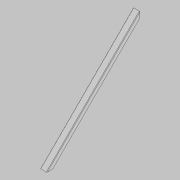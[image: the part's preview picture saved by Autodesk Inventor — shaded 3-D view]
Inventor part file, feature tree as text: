
AUTODESK INVENTOR PART (.ipt)
format: ipt  version: 2021 (Build 250183000, 183)  size: 105,472 bytes
history: native  units: mm
features: sweep x1, fillet x1, mirror x1, split x1, other x1, sketch x1
ambient origin geometry x8: Origin, YZ Plane, XZ Plane, XY Plane, X Axis, Y Axis, Z Axis, Center Point
bodies: Solid1 (feature_tree)
feature tree (6):
  sweep  "Sweep1"
  fillet  "Fillet1"  Radius=25.0mm
  mirror  "mirrored45"
  split  "Split1"
  other  "profile"
  sketch  "3D Sketch1"
